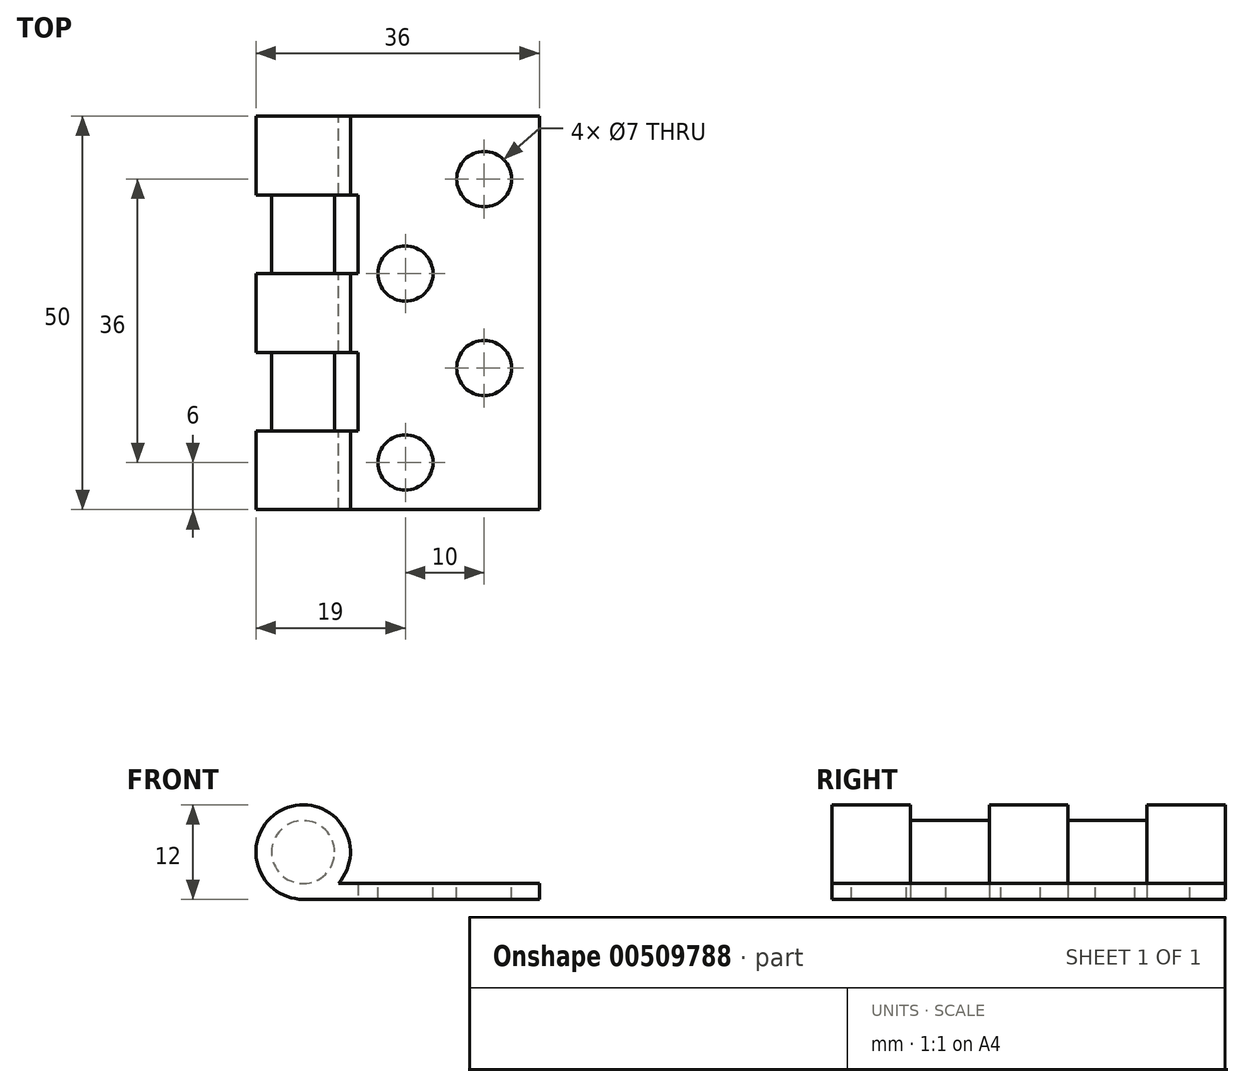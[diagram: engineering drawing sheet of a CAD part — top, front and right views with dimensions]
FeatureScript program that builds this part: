
annotation { "Feature Type Name" : "Feature", "Feature Type Description" : "" }
export const myFeature = defineFeature(function(context is Context, id is Id, definition is map)
    precondition{}
    {
        {
            var Q0;
            Q0=qCreatedBy(makeId("Front.planeOp"),FACE);
            var sketch = newSketch(context, id + "F0", { "sketchPlane" : qUnion([Q0])});
            skLineSegment(sketch, "E0", {"start": v(0.66, 30.5) * mm, "end": v(26.2, 30.5) * mm});
            skLineSegment(sketch, "E1", {"start": v(26.2, 30.5) * mm, "end": v(26.2, 28.5) * mm});
            skLineSegment(sketch, "E2", {"start": v(26.2, 28.5) * mm, "end": v(-3.8, 28.5) * mm});
            skArc(sketch, "E3", {"start": v(0.66, 30.5) * mm, "mid": v(-6.26, 39.98) * mm, "end": v(-3.8, 28.5) * mm});
            skCircle(sketch, "E4", {"center": v(-3.8, 34.5) * mm, "radius": 4 * mm});
            skSolve(sketch);
        }
        {
            var Q0;
            Q0 = qSketchRegion(id + "F0", true);
            extrude(context, id + "F1", {"entities" : qUnion([Q0]), "depth" : 50 * mm});
        }
        {
            var Q0;
            Q0=makeQuery(id+"F1.opExtrude","SWEPT_FACE",FACE,{"disambiguationData":[OSD([sQuery(id+"F0.wireOp",EDGE,"E0")])]});
            var sketch = newSketch(context, id + "F2", { "sketchPlane" : qUnion([Q0])});
            skCircle(sketch, "E5", {"center": v(19.2, -8) * mm, "radius": 3.5 * mm});
            skCircle(sketch, "E6", {"center": v(19.2, -32) * mm, "radius": 3.5 * mm});
            skCircle(sketch, "E7", {"center": v(9.2, -20) * mm, "radius": 3.5 * mm});
            skCircle(sketch, "E8", {"center": v(9.2, -44) * mm, "radius": 3.5 * mm});
            skSolve(sketch);
        }
        {
            var Q0;
            Q0=makeQuery(id+"F2.imprint","IMPRINT",FACE,{"disambiguationData":[TD([[makeQuery(id+"F2.imprint","IMPRINT",EDGE,{"derivedFrom":sQuery(id+"F2.wireOp",EDGE,"E6")}),1.0]])]});
            var Q1;
            Q1=makeQuery(id+"F2.imprint","IMPRINT",FACE,{"disambiguationData":[TD([[makeQuery(id+"F2.imprint","IMPRINT",EDGE,{"derivedFrom":sQuery(id+"F2.wireOp",EDGE,"E8")}),1.0]])]});
            var Q2;
            Q2=makeQuery(id+"F2.imprint","IMPRINT",FACE,{"disambiguationData":[TD([[makeQuery(id+"F2.imprint","IMPRINT",EDGE,{"derivedFrom":sQuery(id+"F2.wireOp",EDGE,"E7")}),1.0]])]});
            var Q3;
            Q3=makeQuery(id+"F2.imprint","IMPRINT",FACE,{"disambiguationData":[TD([[makeQuery(id+"F2.imprint","IMPRINT",EDGE,{"derivedFrom":sQuery(id+"F2.wireOp",EDGE,"E5")}),1.0]])]});
            extrude(context, id + "F3", {"entities" : qUnion([Q0, Q1, Q2, Q3]), "operationType" : NewBodyOperationType.REMOVE, "endBound" : BoundingType.THROUGH_ALL, "oppositeDirection" : true, "depth" : 25 * mm});
        }
        {
            var Q0;
            Q0=makeQuery(id+"F1.opExtrude","SWEPT_FACE",FACE,{"disambiguationData":[OSD([sQuery(id+"F0.wireOp",EDGE,"E2")])]});
            var sketch = newSketch(context, id + "F4", { "sketchPlane" : qUnion([Q0])});
            skLineSegment(sketch, "E9.bottom", {"start": v(3.2, 40) * mm, "end": v(-11.8, 40) * mm});
            skLineSegment(sketch, "E9.top", {"start": v(3.2, 30) * mm, "end": v(-11.8, 30) * mm});
            skLineSegment(sketch, "E9.left", {"start": v(3.2, 40) * mm, "end": v(3.2, 30) * mm});
            skLineSegment(sketch, "E9.right", {"start": v(-11.8, 40) * mm, "end": v(-11.8, 30) * mm});
            skLineSegment(sketch, "E10.bottom", {"start": v(3.2, 20) * mm, "end": v(-11.8, 20) * mm});
            skLineSegment(sketch, "E10.top", {"start": v(3.2, 10) * mm, "end": v(-11.8, 10) * mm});
            skLineSegment(sketch, "E10.left", {"start": v(3.2, 20) * mm, "end": v(3.2, 10) * mm});
            skLineSegment(sketch, "E10.right", {"start": v(-11.8, 20) * mm, "end": v(-11.8, 10) * mm});
            skSolve(sketch);
        }
        {
            var Q0;
            Q0 = qSketchRegion(id + "F4", true);
            extrude(context, id + "F5", {"entities" : qUnion([Q0]), "operationType" : NewBodyOperationType.REMOVE, "oppositeDirection" : true, "depth" : 25 * mm});
        }
        {
            var Q0;
            Q0=makeQuery(id+"F1.opExtrude","CAP_FACE",FACE,{"disambiguationData":[OSD([sQuery(id+"F0.wireOp",EDGE,"E0"),sQuery(id+"F0.wireOp",EDGE,"E1"),sQuery(id+"F0.wireOp",EDGE,"E2"),sQuery(id+"F0.wireOp",EDGE,"E3"),sQuery(id+"F0.wireOp",EDGE,"E4")])],"isStart":true});
            var sketch = newSketch(context, id + "F6", { "sketchPlane" : qUnion([Q0])});
            skCircle(sketch, "E11", {"center": v(3.8, 34.5) * mm, "radius": 4 * mm});
            skSolve(sketch);
        }
        {
            var Q0;
            Q0 = qSketchRegion(id + "F6", true);
            extrude(context, id + "F7", {"entities" : qUnion([Q0]), "operationType" : NewBodyOperationType.ADD, "oppositeDirection" : true, "depth" : 50 * mm});
        }
    });
